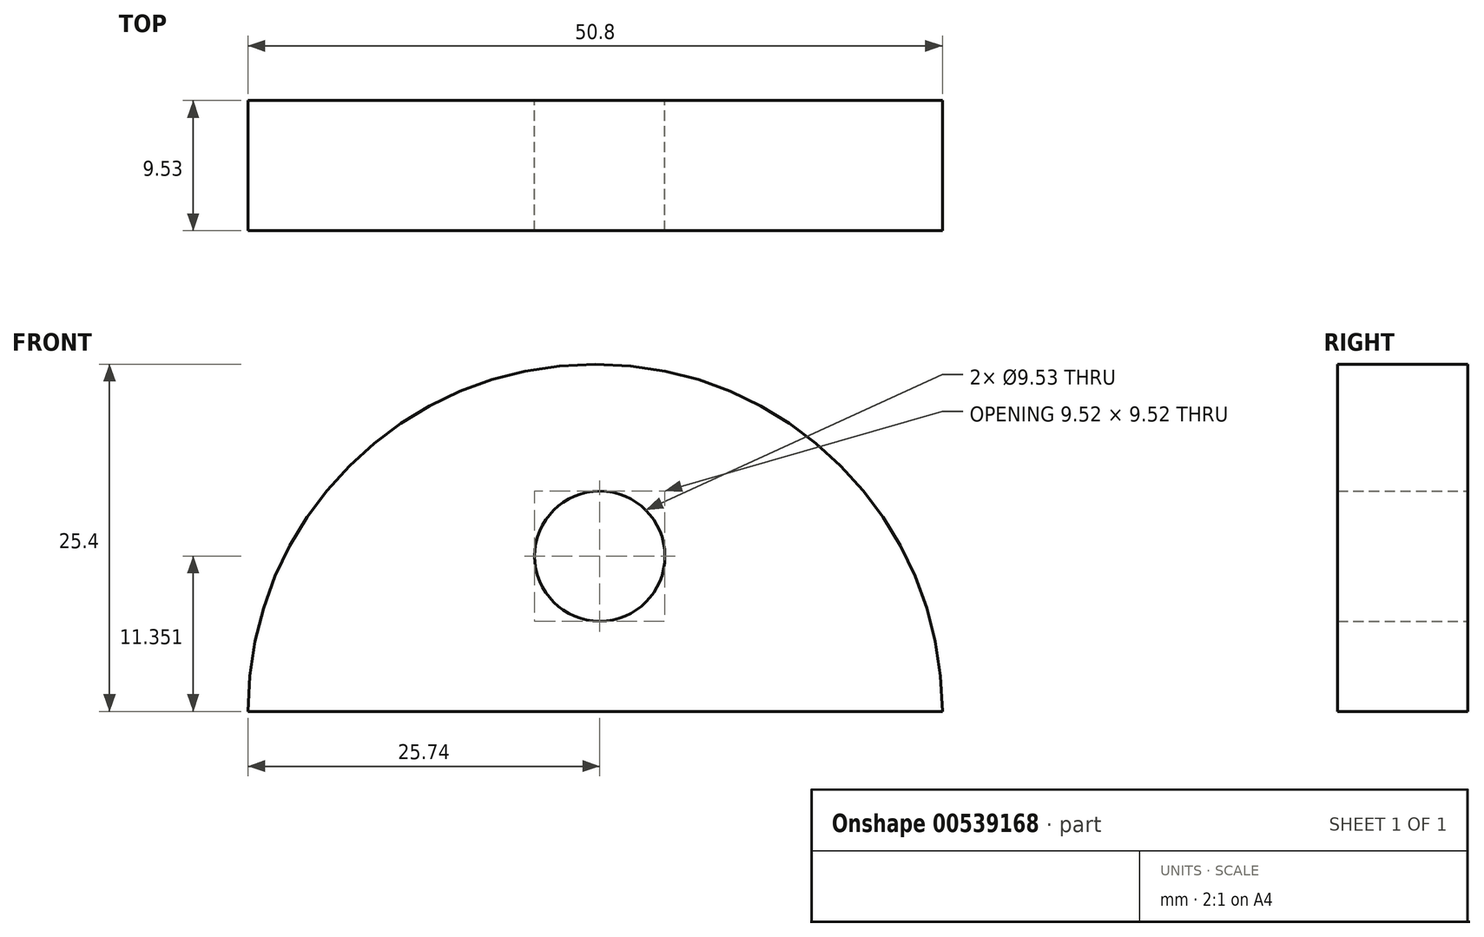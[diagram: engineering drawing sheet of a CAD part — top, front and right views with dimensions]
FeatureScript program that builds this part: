
annotation { "Feature Type Name" : "Feature", "Feature Type Description" : "" }
export const myFeature = defineFeature(function(context is Context, id is Id, definition is map)
    precondition{}
    {
        {
            var Q0;
            Q0=qCreatedBy(makeId("Front.planeOp"),FACE);
            var sketch = newSketch(context, id + "F0", { "sketchPlane" : qUnion([Q0])});
            skArc(sketch, "E0", {"start": v(50.8, 0) * mm, "mid": v(25.4, 25.4) * mm, "end": v(0, 0) * mm});
            skLineSegment(sketch, "E1", {"start": v(0, 0) * mm, "end": v(50.8, 0) * mm});
            skSolve(sketch);
        }
        {
            var Q0;
            Q0=makeQuery(id+"F0.imprint","IMPRINT",FACE,{"disambiguationData":[TD([[makeQuery(id+"F0.imprint","IMPRINT",EDGE,{"derivedFrom":sQuery(id+"F0.wireOp",EDGE,"E0")}),1.0]])]});
            extrude(context, id + "F1", {"entities" : qUnion([Q0]), "depth" : 9.52 * mm, "offsetDistance" : 25.4 * mm});
        }
        {
            var Q0;
            Q0=qCreatedBy(makeId("Front.planeOp"),FACE);
            var sketch = newSketch(context, id + "F2", { "sketchPlane" : qUnion([Q0])});
            skCircle(sketch, "E2", {"center": v(25.74, 11.35) * mm, "radius": 4.76 * mm});
            skSolve(sketch);
        }
        {
            var Q0;
            Q0=sQuery(id+"F2.wireOp",VERTEX,"E2.center");
            var Q1;
            Q1=makeQuery(id+"F1.opExtrude","SWEPT_BODY",BODY,{"disambiguationData":[OSD([sQuery(id+"F0.wireOp",EDGE,"E0"),sQuery(id+"F0.wireOp",EDGE,"E1")])]});
            hole(context, id + "F3", {"style" : HoleStyle.SIMPLE, "endStyle" : HoleEndStyle.THROUGH, "oppositeDirection" : true, "holeDiameter" : 9.52 * mm, "isTappedThrough" : true, "tappedDepth" : 12.7 * mm, "tapClearance" : 3, "locations" : qUnion([Q0]), "scope" : qUnion([Q1])});
        }
    });
